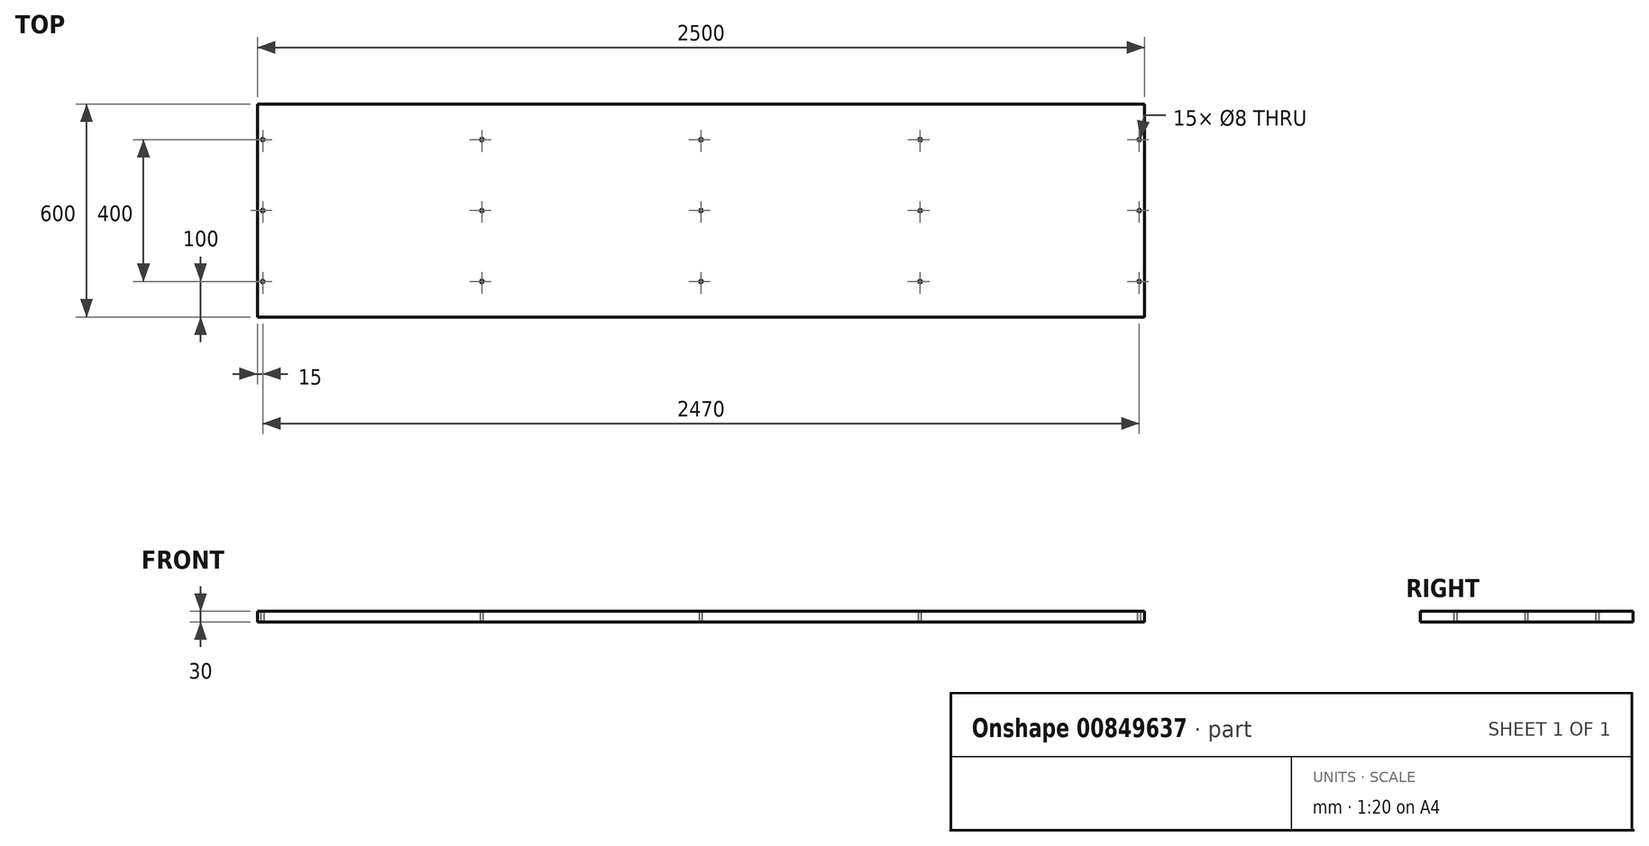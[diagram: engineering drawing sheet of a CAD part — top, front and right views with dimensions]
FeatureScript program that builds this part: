
annotation { "Feature Type Name" : "Feature", "Feature Type Description" : "" }
export const myFeature = defineFeature(function(context is Context, id is Id, definition is map)
    precondition{}
    {
        {
            var Q0;
            Q0=qCreatedBy(makeId("Top.planeOp"),FACE);
            var sketch = newSketch(context, id + "F0", { "sketchPlane" : qUnion([Q0])});
            skLineSegment(sketch, "E0.bottom", {"start": v(-1250, 300) * mm, "end": v(1250, 300) * mm});
            skLineSegment(sketch, "E0.top", {"start": v(-1250, -300) * mm, "end": v(1250, -300) * mm});
            skLineSegment(sketch, "E0.left", {"start": v(-1250, 300) * mm, "end": v(-1250, -300) * mm});
            skLineSegment(sketch, "E0.right", {"start": v(1250, 300) * mm, "end": v(1250, -300) * mm});
            skSolve(sketch);
        }
        {
            var Q0;
            Q0=makeQuery(id+"F0.imprint","IMPRINT",FACE,{"disambiguationData":[TD([[makeQuery(id+"F0.imprint","IMPRINT",EDGE,{"derivedFrom":sQuery(id+"F0.wireOp",EDGE,"E0.bottom")}),-1.0]])]});
            extrude(context, id + "F1", {"entities" : qUnion([Q0]), "endBound" : BoundingType.SYMMETRIC, "depth" : 30 * mm, "offsetDistance" : 25 * mm});
        }
        {
            var Q0;
            Q0=makeQuery(id+"F1.opExtrude","CAP_FACE",FACE,{"disambiguationData":[OSD([sQuery(id+"F0.wireOp",EDGE,"E0.bottom"),sQuery(id+"F0.wireOp",EDGE,"E0.top"),sQuery(id+"F0.wireOp",EDGE,"E0.left"),sQuery(id+"F0.wireOp",EDGE,"E0.right")])],"isStart":false});
            var sketch = newSketch(context, id + "F2", { "sketchPlane" : qUnion([Q0])});
            skPoint(sketch, "E1", {"position": v(-1235, 200) * mm});
            skPoint(sketch, "E2", {"position": v(-1235, 0) * mm});
            skPoint(sketch, "E3", {"position": v(-1235, -200) * mm});
            skPoint(sketch, "E4", {"position": v(1235, 200) * mm});
            skPoint(sketch, "E5", {"position": v(1235, 0) * mm});
            skPoint(sketch, "E6", {"position": v(1235, -200) * mm});
            skPoint(sketch, "E7", {"position": v(0, 200) * mm});
            skPoint(sketch, "E8", {"position": v(0, 0) * mm});
            skPoint(sketch, "E9", {"position": v(0, -200) * mm});
            skPoint(sketch, "E10", {"position": v(-617.5, 200) * mm});
            skPoint(sketch, "E11", {"position": v(-617.5, 0) * mm});
            skPoint(sketch, "E12", {"position": v(-617.5, -200) * mm});
            skPoint(sketch, "E13", {"position": v(617.5, 200) * mm});
            skPoint(sketch, "E14", {"position": v(617.5, 0) * mm});
            skPoint(sketch, "E15", {"position": v(617.5, -200) * mm});
            skSolve(sketch);
        }
        {
            var Q0;
            Q0=sQuery(id+"F2.wireOp",VERTEX,"E1");
            var Q1;
            Q1=sQuery(id+"F2.wireOp",VERTEX,"E2");
            var Q2;
            Q2=sQuery(id+"F2.wireOp",VERTEX,"E3");
            var Q3;
            Q3=sQuery(id+"F2.wireOp",VERTEX,"E10");
            var Q4;
            Q4=sQuery(id+"F2.wireOp",VERTEX,"E11");
            var Q5;
            Q5=sQuery(id+"F2.wireOp",VERTEX,"E12");
            var Q6;
            Q6=sQuery(id+"F2.wireOp",VERTEX,"E7");
            var Q7;
            Q7=sQuery(id+"F2.wireOp",VERTEX,"E8");
            var Q8;
            Q8=sQuery(id+"F2.wireOp",VERTEX,"E9");
            var Q9;
            Q9=sQuery(id+"F2.wireOp",VERTEX,"E13");
            var Q10;
            Q10=sQuery(id+"F2.wireOp",VERTEX,"E14");
            var Q11;
            Q11=sQuery(id+"F2.wireOp",VERTEX,"E4");
            var Q12;
            Q12=sQuery(id+"F2.wireOp",VERTEX,"E5");
            var Q13;
            Q13=sQuery(id+"F2.wireOp",VERTEX,"E6");
            var Q14;
            Q14=sQuery(id+"F2.wireOp",VERTEX,"E15");
            var Q15;
            Q15=makeQuery(id+"F1.opExtrude","SWEPT_BODY",BODY,{"disambiguationData":[OSD([sQuery(id+"F0.wireOp",EDGE,"E0.bottom"),sQuery(id+"F0.wireOp",EDGE,"E0.top"),sQuery(id+"F0.wireOp",EDGE,"E0.left"),sQuery(id+"F0.wireOp",EDGE,"E0.right")])]});
            hole(context, id + "F3", {"style" : HoleStyle.SIMPLE, "endStyle" : HoleEndStyle.BLIND, "holeDiameter" : 8 * mm, "majorDiameter" : 5 * mm, "holeDepth" : 30 * mm, "isTappedThrough" : true, "tappedDepth" : 12 * mm, "tapClearance" : 3, "locations" : qUnion([Q0, Q1, Q2, Q3, Q4, Q5, Q6, Q7, Q8, Q9, Q10, Q11, Q12, Q13, Q14]), "scope" : qUnion([Q15])});
        }
    });
